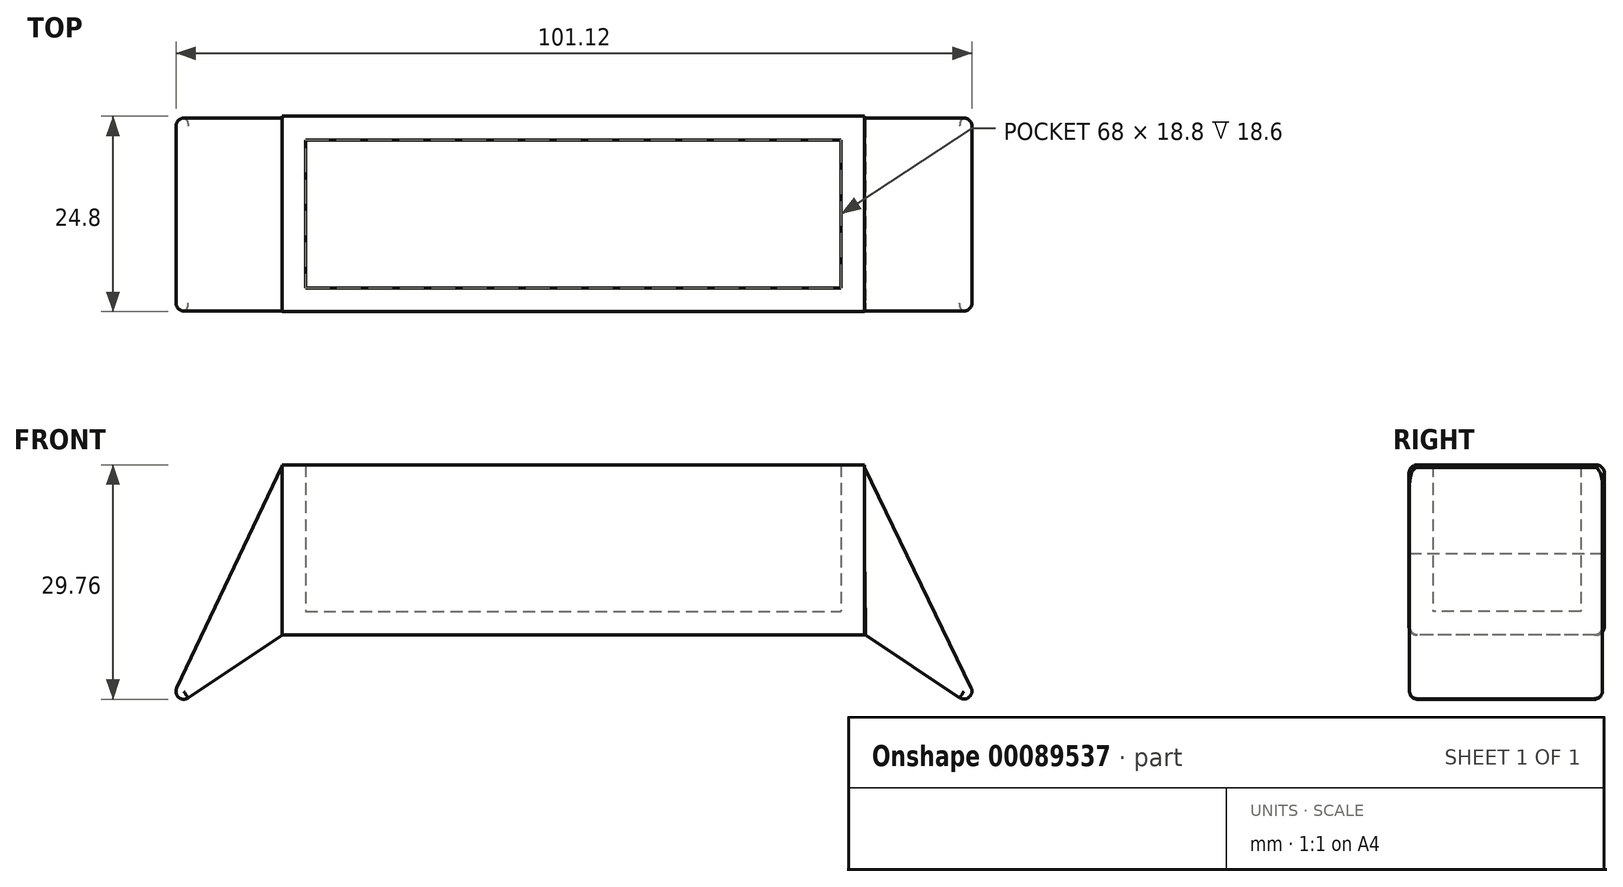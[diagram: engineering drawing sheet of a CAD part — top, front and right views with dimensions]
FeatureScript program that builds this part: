
annotation { "Feature Type Name" : "Feature", "Feature Type Description" : "" }
export const myFeature = defineFeature(function(context is Context, id is Id, definition is map)
    precondition{}
    {
        {
            var Q0;
            Q0=qCreatedBy(makeId("Top.planeOp"),FACE);
            var sketch = newSketch(context, id + "F0", { "sketchPlane" : qUnion([Q0])});
            skLineSegment(sketch, "E0.bottom", {"start": v(-30.96, 10.74) * mm, "end": v(37.04, 10.74) * mm});
            skLineSegment(sketch, "E0.top", {"start": v(-30.96, -8.06) * mm, "end": v(37.04, -8.06) * mm});
            skLineSegment(sketch, "E0.left", {"start": v(-30.96, 10.74) * mm, "end": v(-30.96, -8.06) * mm});
            skLineSegment(sketch, "E0.right", {"start": v(37.04, 10.74) * mm, "end": v(37.04, -8.06) * mm});
            skLineSegment(sketch, "E1.bottom", {"start": v(-33.96, 13.74) * mm, "end": v(40.04, 13.74) * mm});
            skLineSegment(sketch, "E1.top", {"start": v(-33.96, -11.06) * mm, "end": v(40.04, -11.06) * mm});
            skLineSegment(sketch, "E1.left", {"start": v(-33.96, 13.74) * mm, "end": v(-33.96, -11.06) * mm});
            skLineSegment(sketch, "E1.right", {"start": v(40.04, 13.74) * mm, "end": v(40.04, -11.06) * mm});
            skLineSegment(sketch, "E2", {"start": v(37.04, 10.74) * mm, "end": v(3.04, 10.74) * mm});
            skSolve(sketch);
        }
        {
            var Q0;
            Q0=makeQuery(id+"F0.imprint","IMPRINT",FACE,{"disambiguationData":[TD([[makeQuery(id+"F0.imprint","IMPRINT",EDGE,{"derivedFrom":sQuery(id+"F0.wireOp",EDGE,"E0.bottom")}),1.0]])]});
            extrude(context, id + "F1", {"entities" : qUnion([Q0]), "depth" : 21.6 * mm});
        }
        {
            var Q0;
            Q0=makeQuery(id+"F0.imprint","IMPRINT",FACE,{"disambiguationData":[TD([[makeQuery(id+"F0.imprint","IMPRINT",EDGE,{"derivedFrom":sQuery(id+"F0.wireOp",EDGE,"E0.bottom")}),-1.0]])]});
            extrude(context, id + "F2", {"entities" : qUnion([Q0]), "operationType" : NewBodyOperationType.ADD, "depth" : 3 * mm});
        }
        {
            var Q0;
            Q0=qCreatedBy(makeId("Front.planeOp"),FACE);
            var sketch = newSketch(context, id + "F3", { "sketchPlane" : qUnion([Q0])});
            skLineSegment(sketch, "E3", {"start": v(-33.9, 0) * mm, "end": v(-48.9, 0) * mm, "construction": true});
            skLineSegment(sketch, "E4", {"start": v(-48.9, 0) * mm, "end": v(-48.9, -10) * mm, "construction": true});
            skLineSegment(sketch, "E5", {"start": v(-48.9, -10) * mm, "end": v(-33.9, 0) * mm});
            skLineSegment(sketch, "E6", {"start": v(-48.9, -10) * mm, "end": v(-33.9, 21.6) * mm});
            skLineSegment(sketch, "E7", {"start": v(-33.9, 21.6) * mm, "end": v(-33.9, 0) * mm});
            skLineSegment(sketch, "E8", {"start": v(40.16, 0) * mm, "end": v(55.16, 0) * mm, "construction": true});
            skLineSegment(sketch, "E9", {"start": v(55.16, 0) * mm, "end": v(55.16, -10) * mm, "construction": true});
            skLineSegment(sketch, "E10", {"start": v(40.16, 0) * mm, "end": v(55.16, -10) * mm});
            skLineSegment(sketch, "E11", {"start": v(55.16, -10) * mm, "end": v(39.91, 21.57) * mm});
            skLineSegment(sketch, "E12", {"start": v(39.91, 21.57) * mm, "end": v(40.16, 0) * mm});
            skSolve(sketch);
        }
        {
            var Q0;
            Q0=makeQuery(id+"F3.imprint","IMPRINT",FACE,{"disambiguationData":[TD([[makeQuery(id+"F3.imprint","IMPRINT",EDGE,{"derivedFrom":sQuery(id+"F3.wireOp",EDGE,"E5")}),1.0]])]});
            var Q1;
            Q1=makeQuery(id+"F3.imprint","IMPRINT",FACE,{"disambiguationData":[TD([[makeQuery(id+"F3.imprint","IMPRINT",EDGE,{"derivedFrom":sQuery(id+"F3.wireOp",EDGE,"E10")}),1.0]])]});
            extrude(context, id + "F4", {"entities" : qUnion([Q0, Q1]), "operationType" : NewBodyOperationType.ADD, "oppositeDirection" : true, "depth" : 13.5 * mm, "hasSecondDirection" : true, "secondDirectionOppositeDirection" : false, "secondDirectionDepth" : 11 * mm});
        }
        {
            var Q0;
            Q0=makeQuery(id+"F1.opExtrude","CAP_EDGE",EDGE,{"disambiguationData":[OSD([sQuery(id+"F0.wireOp",EDGE,"E1.top")])],"isStart":true});
            fillet(context, id + "F5", {"entities" : qUnion([Q0]), "radius" : 1 * mm, "tangentPropagation" : true, "allowEdgeOverflow" : false});
        }
        {
            var Q0;
            Q0=makeQuery(id+"F4.opExtrude","CAP_EDGE",EDGE,{"disambiguationData":[OSD([sQuery(id+"F3.wireOp",EDGE,"E5")])],"isStart":true});
            fillet(context, id + "F6", {"entities" : qUnion([Q0]), "radius" : 1 * mm, "tangentPropagation" : true, "allowEdgeOverflow" : false});
        }
        {
            var Q0;
            Q0=makeQuery(id+"F4.opExtrude","CAP_EDGE",EDGE,{"disambiguationData":[OSD([sQuery(id+"F3.wireOp",EDGE,"E10")])],"isStart":true});
            fillet(context, id + "F7", {"entities" : qUnion([Q0]), "radius" : 1 * mm, "tangentPropagation" : true, "allowEdgeOverflow" : false});
        }
        {
            var Q0;
            Q0=makeQuery(id+"F1.opExtrude","CAP_EDGE",EDGE,{"disambiguationData":[OSD([sQuery(id+"F0.wireOp",EDGE,"E1.bottom")])],"isStart":true});
            fillet(context, id + "F8", {"entities" : qUnion([Q0]), "radius" : 1 * mm, "tangentPropagation" : true, "allowEdgeOverflow" : false});
        }
        {
            var Q0;
            Q0=makeQuery(id+"F4.opExtrude","CAP_EDGE",EDGE,{"disambiguationData":[OSD([sQuery(id+"F3.wireOp",EDGE,"E5")])],"isStart":false});
            var Q1;
            Q1=makeQuery(id+"F4.opExtrude","CAP_EDGE",EDGE,{"disambiguationData":[OSD([sQuery(id+"F3.wireOp",EDGE,"E10")])],"isStart":false});
            fillet(context, id + "F9", {"entities" : qUnion([Q0, Q1]), "radius" : 1 * mm, "tangentPropagation" : true, "allowEdgeOverflow" : false});
        }
        {
            var Q0;
            Q0=makeQuery(id+"F4.opExtrude","CAP_EDGE",EDGE,{"disambiguationData":[OSD([sQuery(id+"F3.wireOp",EDGE,"E11")])],"isStart":false});
            fillet(context, id + "F10", {"entities" : qUnion([Q0]), "radius" : 1 * mm, "tangentPropagation" : true, "allowEdgeOverflow" : false});
        }
        {
            var Q0;
            Q0=makeQuery(id+"F4.opExtrude","CAP_EDGE",EDGE,{"disambiguationData":[OSD([sQuery(id+"F3.wireOp",EDGE,"E6")])],"isStart":false});
            fillet(context, id + "F11", {"entities" : qUnion([Q0]), "radius" : 1 * mm, "tangentPropagation" : true, "allowEdgeOverflow" : false});
        }
        {
            var Q0;
            Q0=makeQuery(id+"F1.opExtrude","CAP_EDGE",EDGE,{"disambiguationData":[OSD([sQuery(id+"F0.wireOp",EDGE,"E1.bottom")])],"isStart":false});
            fillet(context, id + "F12", {"entities" : qUnion([Q0]), "radius" : 1 * mm, "tangentPropagation" : true, "allowEdgeOverflow" : false});
        }
        {
            var Q0;
            Q0=makeQuery(id+"F1.opExtrude","CAP_EDGE",EDGE,{"disambiguationData":[OSD([sQuery(id+"F0.wireOp",EDGE,"E1.top")])],"isStart":false});
            fillet(context, id + "F13", {"entities" : qUnion([Q0]), "radius" : 1 * mm, "tangentPropagation" : true, "allowEdgeOverflow" : false});
        }
    });
